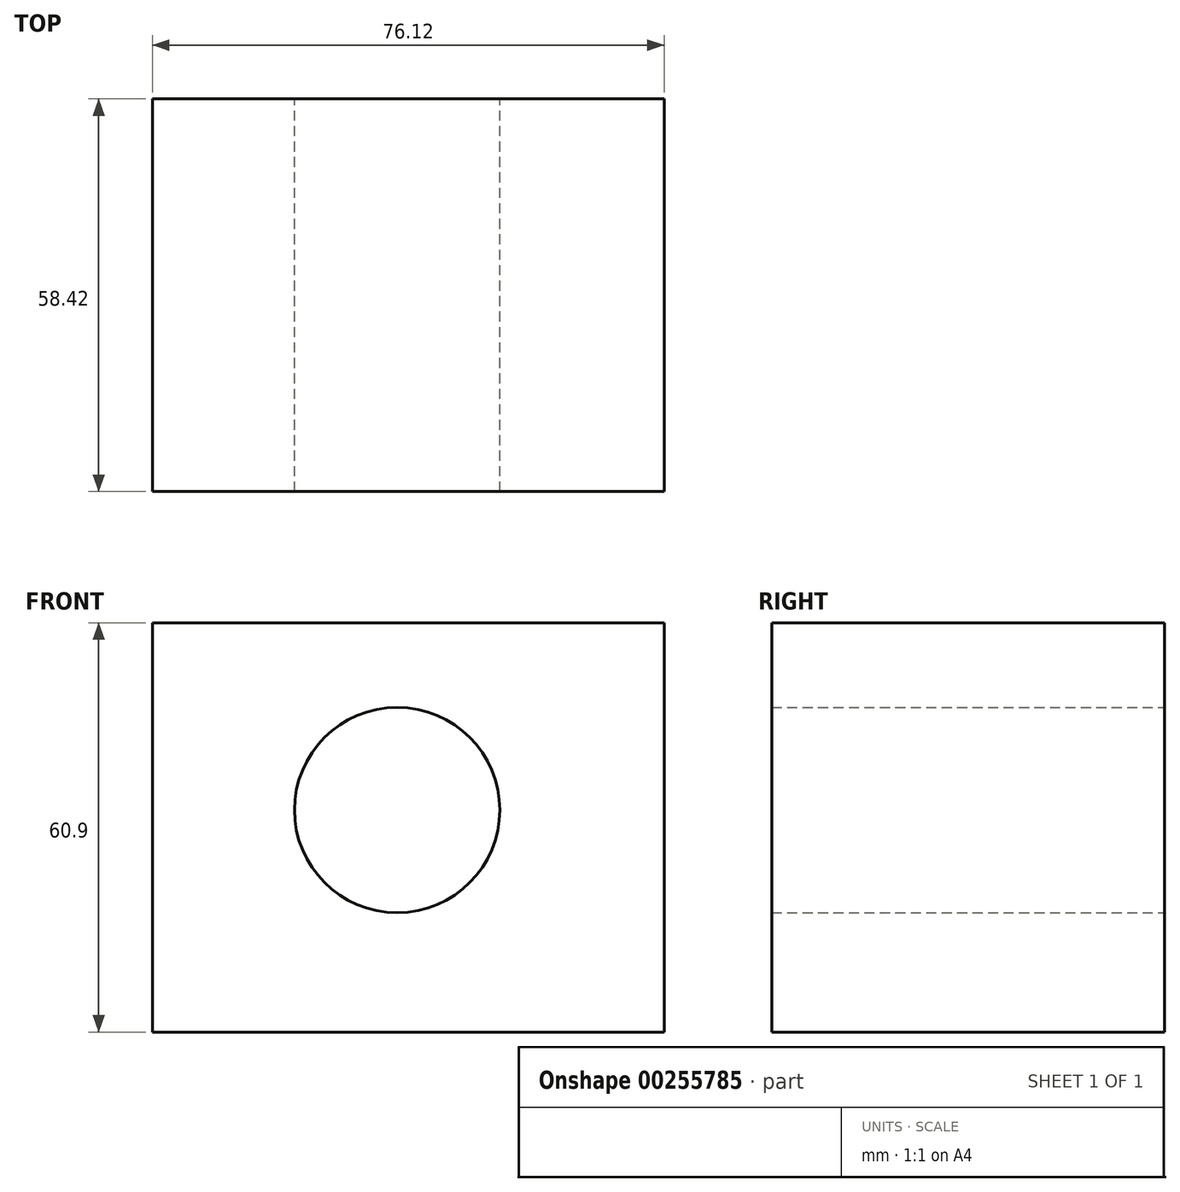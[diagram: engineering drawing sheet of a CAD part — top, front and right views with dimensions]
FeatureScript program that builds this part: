
annotation { "Feature Type Name" : "Feature", "Feature Type Description" : "" }
export const myFeature = defineFeature(function(context is Context, id is Id, definition is map)
    precondition{}
    {
        {
            var Q0;
            Q0=qCreatedBy(makeId("Front.planeOp"),FACE);
            var sketch = newSketch(context, id + "F0", { "sketchPlane" : qUnion([Q0])});
            skLineSegment(sketch, "E0.bottom", {"start": v(-36.4, 27.87) * mm, "end": v(39.72, 27.87) * mm});
            skLineSegment(sketch, "E0.top", {"start": v(-36.4, -33.03) * mm, "end": v(39.72, -33.03) * mm});
            skLineSegment(sketch, "E0.left", {"start": v(-36.4, 27.87) * mm, "end": v(-36.4, -33.03) * mm});
            skLineSegment(sketch, "E0.right", {"start": v(39.72, 27.87) * mm, "end": v(39.72, -33.03) * mm});
            skCircle(sketch, "E1", {"center": v(0, 0) * mm, "radius": 15.27 * mm});
            skSolve(sketch);
        }
        {
            var Q0;
            Q0 = qSketchRegion(id + "F0", true);
            extrude(context, id + "F1", {"entities" : qUnion([Q0]), "depth" : 58.42 * mm});
        }
    });
